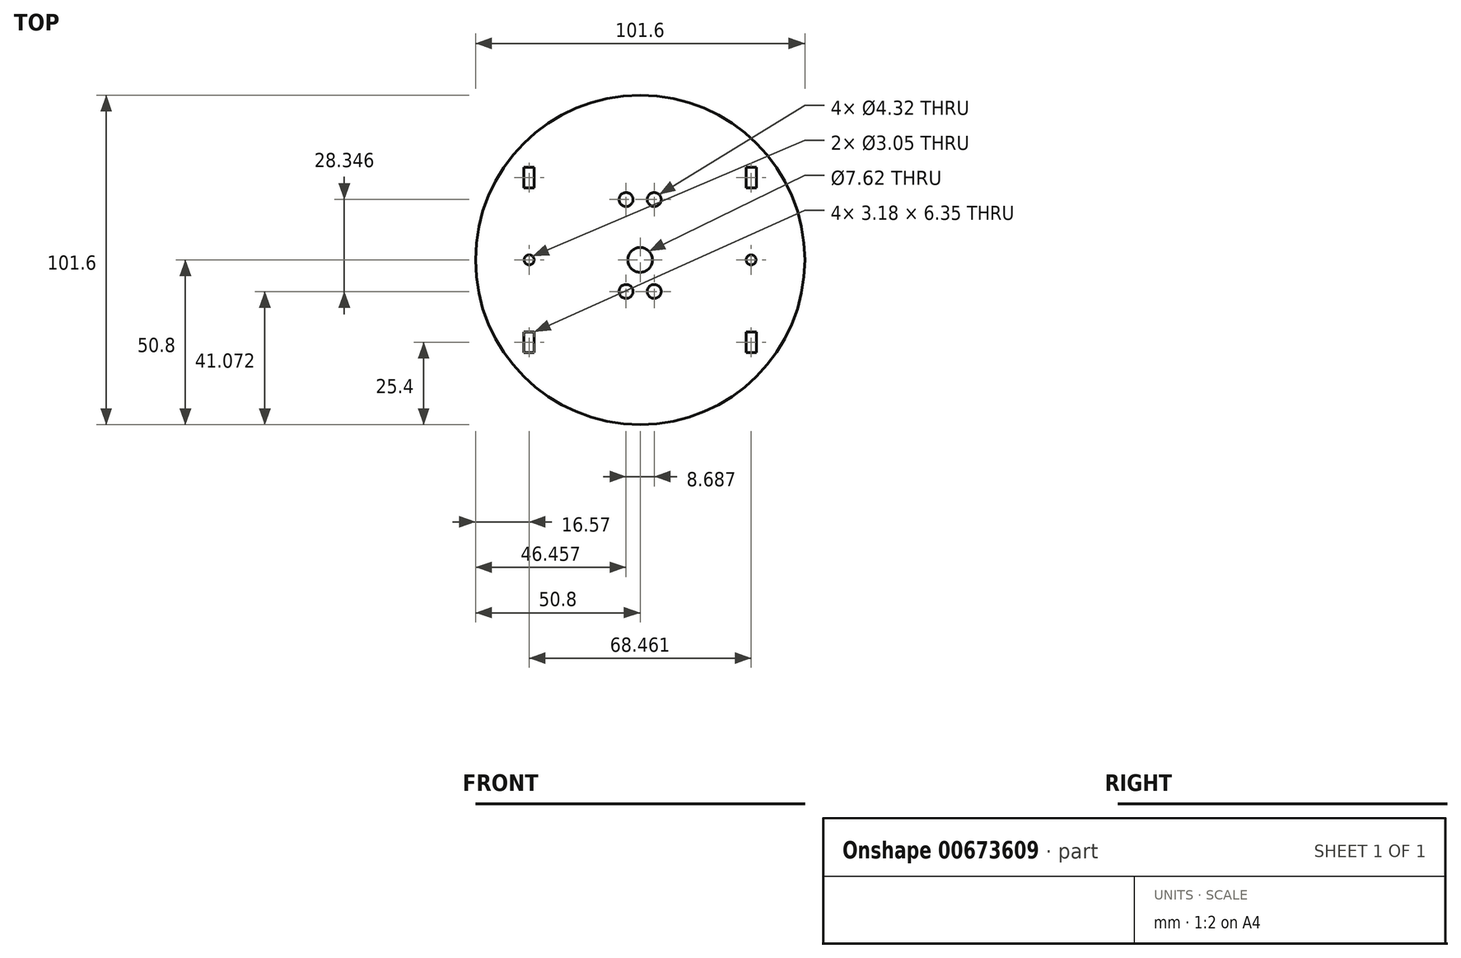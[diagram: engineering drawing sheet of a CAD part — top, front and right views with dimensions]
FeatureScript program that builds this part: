
annotation { "Feature Type Name" : "Feature", "Feature Type Description" : "" }
export const myFeature = defineFeature(function(context is Context, id is Id, definition is map)
    precondition{}
    {
        {
            var Q0;
            Q0=qCreatedBy(makeId("Top.planeOp"),FACE);
            var sketch = newSketch(context, id + "F0", { "sketchPlane" : qUnion([Q0])});
            skArc(sketch, "E0", {"start": v(-50.4, -6.34) * mm, "mid": v(-35.92, -35.92) * mm, "end": v(-6.34, -50.4) * mm});
            skArc(sketch, "E1.trimOffspring", {"start": v(-6.34, 50.4) * mm, "mid": v(-35.92, 35.92) * mm, "end": v(-50.4, 6.34) * mm});
            skArc(sketch, "E2.trimOffspring", {"start": v(50.4, 6.34) * mm, "mid": v(35.92, 35.92) * mm, "end": v(6.34, 50.4) * mm});
            skArc(sketch, "E3.trimOffspring", {"start": v(6.34, -50.4) * mm, "mid": v(35.92, -35.92) * mm, "end": v(50.4, -6.34) * mm});
            skLineSegment(sketch, "E4", {"start": v(0, 0) * mm, "end": v(34.23, 0) * mm, "construction": true});
            skLineSegment(sketch, "E5", {"start": v(34.23, 0) * mm, "end": v(34.23, 25.4) * mm, "construction": true});
            skLineSegment(sketch, "E6.bottom", {"start": v(35.82, 22.23) * mm, "end": v(32.64, 22.23) * mm});
            skLineSegment(sketch, "E6.top", {"start": v(35.82, 28.58) * mm, "end": v(32.64, 28.58) * mm});
            skLineSegment(sketch, "E6.left", {"start": v(35.82, 22.23) * mm, "end": v(35.82, 28.58) * mm});
            skLineSegment(sketch, "E6.right", {"start": v(32.64, 22.23) * mm, "end": v(32.64, 28.58) * mm});
            skPoint(sketch, "E6.middle", {"position": v(34.23, 25.4) * mm});
            skLineSegment(sketch, "E7.MirrorCS", {"start": v(32.64, -22.23) * mm, "end": v(32.64, -28.58) * mm});
            skLineSegment(sketch, "E8.MirrorCS", {"start": v(35.82, -28.58) * mm, "end": v(32.64, -28.58) * mm});
            skLineSegment(sketch, "E9.MirrorCS", {"start": v(35.82, -22.23) * mm, "end": v(35.82, -28.58) * mm});
            skLineSegment(sketch, "E10.MirrorCS", {"start": v(35.82, -22.23) * mm, "end": v(32.64, -22.23) * mm});
            skLineSegment(sketch, "E11.MirrorCS", {"start": v(-35.82, 28.58) * mm, "end": v(-32.64, 28.58) * mm});
            skLineSegment(sketch, "E12.MirrorCS", {"start": v(-32.64, 22.23) * mm, "end": v(-32.64, 28.58) * mm});
            skLineSegment(sketch, "E13.MirrorCS", {"start": v(-35.82, 22.23) * mm, "end": v(-32.64, 22.23) * mm});
            skLineSegment(sketch, "E14.MirrorCS", {"start": v(-35.82, 22.23) * mm, "end": v(-35.82, 28.58) * mm});
            skLineSegment(sketch, "E15.MirrorCS", {"start": v(-35.82, -22.23) * mm, "end": v(-32.64, -22.23) * mm});
            skLineSegment(sketch, "E16.MirrorCS", {"start": v(-32.64, -22.23) * mm, "end": v(-32.64, -28.58) * mm});
            skLineSegment(sketch, "E17.MirrorCS", {"start": v(-35.82, -28.58) * mm, "end": v(-32.64, -28.58) * mm});
            skLineSegment(sketch, "E18.MirrorCS", {"start": v(-35.82, -22.23) * mm, "end": v(-35.82, -28.58) * mm});
            skCircle(sketch, "E19", {"center": v(0, 0) * mm, "radius": 50.8 * mm});
            skPoint(sketch, "E20.center.orphan", {"position": v(0, -50.8) * mm});
            skPoint(sketch, "E21.center.orphan", {"position": v(-50.8, 0) * mm});
            skPoint(sketch, "E22.center.orphan", {"position": v(50.8, 0) * mm});
            skPoint(sketch, "E23.center.orphan", {"position": v(0, 50.8) * mm});
            skCircle(sketch, "E24", {"center": v(0, 0) * mm, "radius": 3.81 * mm});
            skLineSegment(sketch, "E25", {"start": v(0, 0) * mm, "end": v(0, 18.62) * mm, "construction": true});
            skLineSegment(sketch, "E26", {"start": v(0, 18.62) * mm, "end": v(-11.57, 18.62) * mm, "construction": true});
            skCircle(sketch, "E27", {"center": v(-4.34, 18.62) * mm, "radius": 2.16 * mm});
            skCircle(sketch, "E28.MirrorC", {"center": v(4.34, 18.62) * mm, "radius": 2.16 * mm});
            skLineSegment(sketch, "E29", {"start": v(0, 0) * mm, "end": v(0, -9.73) * mm, "construction": true});
            skLineSegment(sketch, "E30", {"start": v(0, -9.73) * mm, "end": v(-6.2, -9.73) * mm, "construction": true});
            skCircle(sketch, "E31", {"center": v(-4.34, -9.73) * mm, "radius": 2.16 * mm});
            skCircle(sketch, "E32.MirrorC", {"center": v(4.34, -9.73) * mm, "radius": 2.16 * mm});
            skCircle(sketch, "E33", {"center": v(34.23, 0) * mm, "radius": 1.52 * mm});
            skCircle(sketch, "E34.MirrorC", {"center": v(-34.23, 0) * mm, "radius": 1.52 * mm});
            skSolve(sketch);
        }
        {
            var Q0;
            Q0=makeQuery(id+"F0.imprint","IMPRINT",FACE,{"disambiguationData":[TD([[makeQuery(id+"F0.imprint","IMPRINT",EDGE,{"derivedFrom":sQuery(id+"F0.wireOp",EDGE,"E6.bottom")}),1.0]])]});
            extrude(context, id + "F1", {"entities" : qUnion([Q0]), "depth" : 1 / 203.2 * mm});
        }
    });
